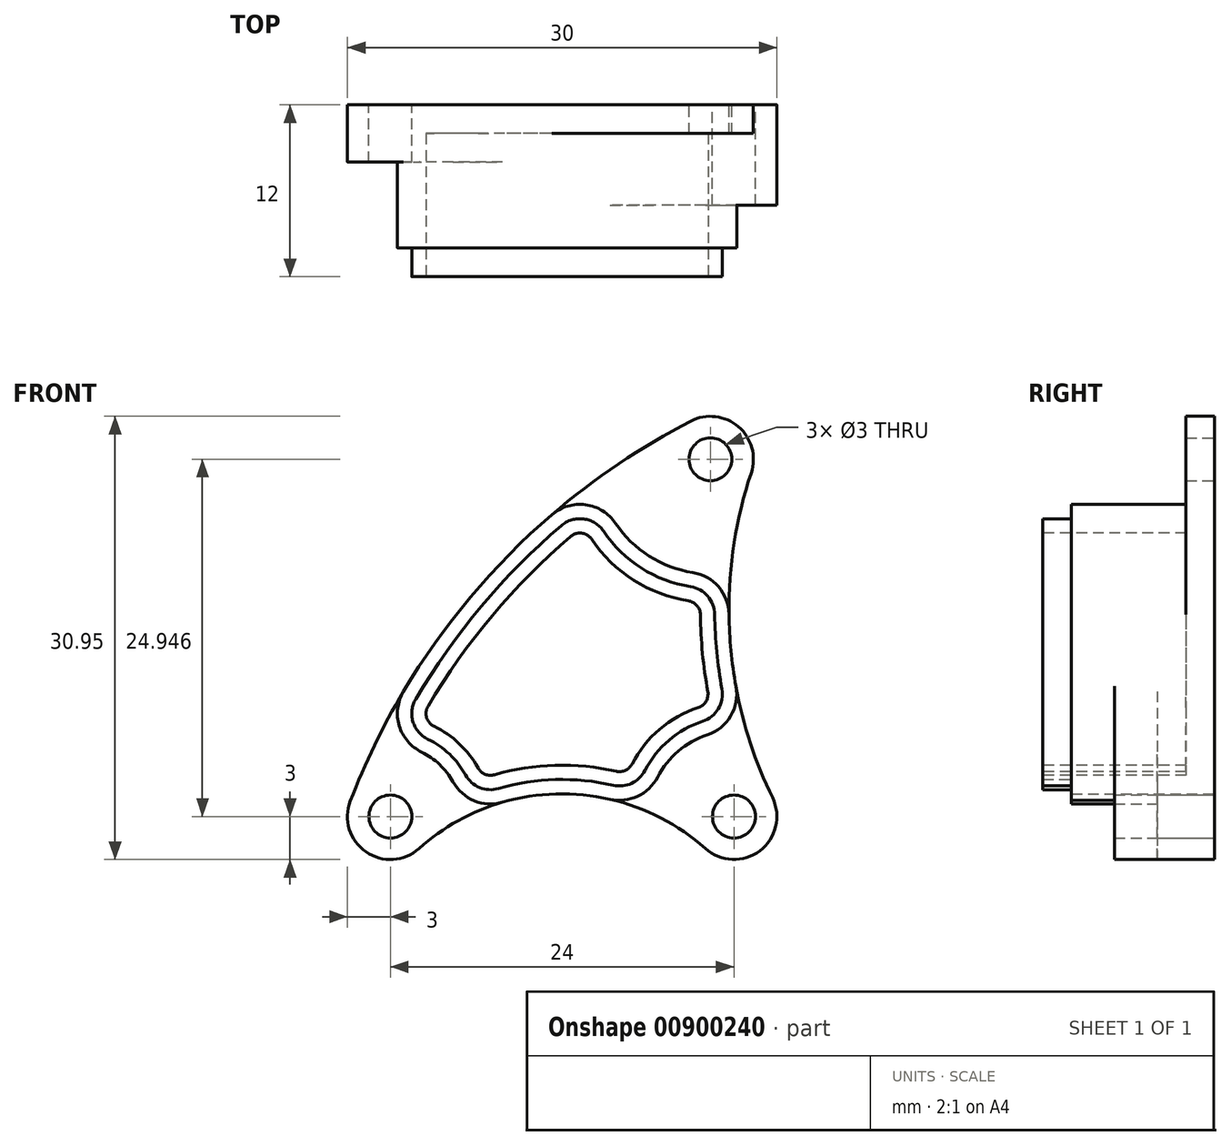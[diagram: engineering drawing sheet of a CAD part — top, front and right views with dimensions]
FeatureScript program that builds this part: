
annotation { "Feature Type Name" : "Feature", "Feature Type Description" : "" }
export const myFeature = defineFeature(function(context is Context, id is Id, definition is map)
    precondition{}
    {
        {
            var Q0;
            Q0=qCreatedBy(makeId("Front.planeOp"),FACE);
            var sketch = newSketch(context, id + "F0", { "sketchPlane" : qUnion([Q0])});
            skArc(sketch, "E0", {"start": v(-2.8, 1.07) * mm, "mid": v(-1.7, -2.47) * mm, "end": v(2, -2.24) * mm});
            skArc(sketch, "E1", {"start": v(25.2, 24) * mm, "mid": v(24.31, 27.22) * mm, "end": v(20.99, 27.61) * mm});
            skArc(sketch, "E2", {"start": v(22, -2.24) * mm, "mid": v(25.8, -2.4) * mm, "end": v(26.7, 1.32) * mm});
            skArc(sketch, "E3", {"start": v(20.99, 27.61) * mm, "mid": v(6.65, 16.54) * mm, "end": v(-2.8, 1.07) * mm});
            skArc(sketch, "E4", {"start": v(22, -2.24) * mm, "mid": v(12, 1.58) * mm, "end": v(2, -2.24) * mm});
            skArc(sketch, "E5", {"start": v(25.2, 24) * mm, "mid": v(23.72, 12.5) * mm, "end": v(26.7, 1.32) * mm});
            skSolve(sketch);
        }
        {
            var Q0;
            Q0=makeQuery(id+"F0.imprint","IMPRINT",FACE,{"disambiguationData":[TD([[makeQuery(id+"F0.imprint","IMPRINT",EDGE,{"derivedFrom":sQuery(id+"F0.wireOp",EDGE,"E0")}),1.0]])]});
            extrude(context, id + "F1", {"entities" : qUnion([Q0]), "depth" : 2 * mm, "offsetDistance" : 25 * mm});
        }
        {
            var Q0;
            Q0=makeQuery(id+"F1.opExtrude","CAP_FACE",FACE,{"disambiguationData":[OSD([sQuery(id+"F0.wireOp",EDGE,"E0"),sQuery(id+"F0.wireOp",EDGE,"E1"),sQuery(id+"F0.wireOp",EDGE,"E2"),sQuery(id+"F0.wireOp",EDGE,"E3"),sQuery(id+"F0.wireOp",EDGE,"E4"),sQuery(id+"F0.wireOp",EDGE,"E5")])],"isStart":false});
            var sketch = newSketch(context, id + "F2", { "sketchPlane" : qUnion([Q0])});
            skArc(sketch, "E6", {"start": v(4.37, 2.42) * mm, "mid": v(3.44, 3.63) * mm, "end": v(2.18, 4.5) * mm});
            skArc(sketch, "E7", {"start": v(22.13, 5.7) * mm, "mid": v(20.1, 4.57) * mm, "end": v(18.67, 2.75) * mm});
            skArc(sketch, "E8", {"start": v(15.72, 20.48) * mm, "mid": v(18.06, 18.2) * mm, "end": v(21.12, 17.04) * mm});
            skArc(sketch, "E9.0", {"start": v(11.28, 21.07) * mm, "mid": v(5.6, 15.32) * mm, "end": v(0.91, 8.73) * mm});
            skArc(sketch, "E10.0", {"start": v(23.66, 14.11) * mm, "mid": v(23.8, 11.6) * mm, "end": v(24.14, 9.09) * mm});
            skArc(sketch, "E11.0", {"start": v(15.34, 1.2) * mm, "mid": v(11.57, 1.58) * mm, "end": v(7.83, 1) * mm});
            skPoint(sketch, "E12.newPointA", {"position": v(-2.8, 1.07) * mm});
            skArc(sketch, "E12.filletArc", {"start": v(0.91, 8.73) * mm, "mid": v(0.62, 6.34) * mm, "end": v(2.18, 4.5) * mm});
            skPoint(sketch, "E13.newPointB", {"position": v(20.99, 27.61) * mm});
            skArc(sketch, "E13.filletArc", {"start": v(15.72, 20.48) * mm, "mid": v(13.64, 21.77) * mm, "end": v(11.28, 21.07) * mm});
            skPoint(sketch, "E14.newPointB", {"position": v(25.2, 24) * mm});
            skArc(sketch, "E14.filletArc", {"start": v(23.66, 14.11) * mm, "mid": v(22.92, 16.04) * mm, "end": v(21.12, 17.04) * mm});
            skPoint(sketch, "E15.newPointA", {"position": v(26.7, 1.32) * mm});
            skArc(sketch, "E15.filletArc", {"start": v(22.13, 5.7) * mm, "mid": v(23.77, 7.02) * mm, "end": v(24.14, 9.09) * mm});
            skPoint(sketch, "E16.newPointB", {"position": v(22, -2.24) * mm});
            skArc(sketch, "E16.filletArc", {"start": v(15.34, 1.2) * mm, "mid": v(17.27, 1.41) * mm, "end": v(18.67, 2.75) * mm});
            skPoint(sketch, "E17.newPointA", {"position": v(2, -2.24) * mm});
            skArc(sketch, "E17.filletArc", {"start": v(4.37, 2.42) * mm, "mid": v(5.85, 1.1) * mm, "end": v(7.83, 1) * mm});
            skSolve(sketch);
        }
        {
            var Q0;
            Q0=makeQuery(id+"F2.imprint","IMPRINT",FACE,{"disambiguationData":[TD([[makeQuery(id+"F2.imprint","IMPRINT",EDGE,{"derivedFrom":sQuery(id+"F2.wireOp",EDGE,"E6")}),-1.0]])]});
            extrude(context, id + "F3", {"entities" : qUnion([Q0]), "operationType" : NewBodyOperationType.ADD, "depth" : 8 * mm, "offsetDistance" : 25 * mm});
        }
        {
            var Q0;
            {var subQ0=sQuery(id+"F0.wireOp",EDGE,"E4");var subQ1=sQuery(id+"F0.wireOp",EDGE,"E3");var subQ2=sQuery(id+"F0.wireOp",EDGE,"E0");Q0=makeQuery(id+"F3.boolean.opBoolean","SPLIT",FACE,{"disambiguationData":[TD([makeQuery(id+"F1.opExtrude","SWEPT_FACE",FACE,{"disambiguationData":[OSD([subQ2])]})])],"derivedFrom":makeQuery(id+"F1.opExtrude","CAP_FACE",FACE,{"disambiguationData":[OSD([subQ2,sQuery(id+"F0.wireOp",EDGE,"E1"),sQuery(id+"F0.wireOp",EDGE,"E2"),subQ1,subQ0,sQuery(id+"F0.wireOp",EDGE,"E5")])],"isStart":false})});}
            var sketch = newSketch(context, id + "F4", { "sketchPlane" : qUnion([Q0])});
            skArc(sketch, "E18.0.0", {"start": v(7.83, 1) * mm, "mid": v(5.85, 1.1) * mm, "end": v(4.37, 2.42) * mm});
            skArc(sketch, "E18.0.1", {"start": v(4.37, 2.42) * mm, "mid": v(3.44, 3.63) * mm, "end": v(2.18, 4.5) * mm});
            skArc(sketch, "E18.0.2", {"start": v(2.18, 4.5) * mm, "mid": v(0.62, 6.34) * mm, "end": v(0.91, 8.73) * mm});
            skArc(sketch, "E18.0.3", {"start": v(0.91, 8.73) * mm, "mid": v(-1.1, 4.98) * mm, "end": v(-2.8, 1.07) * mm});
            skArc(sketch, "E18.0.4", {"start": v(-2.8, 1.07) * mm, "mid": v(-1.7, -2.47) * mm, "end": v(2, -2.24) * mm});
            skArc(sketch, "E18.0.5", {"start": v(2, -2.24) * mm, "mid": v(4.73, -0.3) * mm, "end": v(7.83, 1) * mm});
            skSolve(sketch);
        }
        {
            var Q0;
            Q0=makeQuery(id+"F4.imprint","IMPRINT",FACE,{"disambiguationData":[TD([[makeQuery(id+"F4.imprint","IMPRINT",EDGE,{"derivedFrom":sQuery(id+"F4.wireOp",EDGE,"E18.0.0")}),-1.0]])]});
            extrude(context, id + "F5", {"entities" : qUnion([Q0]), "operationType" : NewBodyOperationType.ADD, "depth" : 2 * mm, "offsetDistance" : 25 * mm});
        }
        {
            var Q0;
            {var subQ0=sQuery(id+"F0.wireOp",EDGE,"E5");var subQ1=sQuery(id+"F0.wireOp",EDGE,"E2");var subQ2=sQuery(id+"F0.wireOp",EDGE,"E4");Q0=makeQuery(id+"F3.boolean.opBoolean","SPLIT",FACE,{"disambiguationData":[TD([makeQuery(id+"F1.opExtrude","SWEPT_FACE",FACE,{"disambiguationData":[OSD([subQ1])]})])],"derivedFrom":makeQuery(id+"F1.opExtrude","CAP_FACE",FACE,{"disambiguationData":[OSD([sQuery(id+"F0.wireOp",EDGE,"E0"),sQuery(id+"F0.wireOp",EDGE,"E1"),subQ1,sQuery(id+"F0.wireOp",EDGE,"E3"),subQ2,subQ0])],"isStart":false})});}
            var sketch = newSketch(context, id + "F6", { "sketchPlane" : qUnion([Q0])});
            skArc(sketch, "E19.0.0", {"start": v(24.14, 9.09) * mm, "mid": v(23.77, 7.02) * mm, "end": v(22.13, 5.7) * mm});
            skArc(sketch, "E19.0.1", {"start": v(22.13, 5.7) * mm, "mid": v(20.1, 4.57) * mm, "end": v(18.67, 2.75) * mm});
            skArc(sketch, "E19.0.2", {"start": v(18.67, 2.75) * mm, "mid": v(17.27, 1.41) * mm, "end": v(15.34, 1.2) * mm});
            skArc(sketch, "E19.0.3", {"start": v(15.34, 1.2) * mm, "mid": v(18.89, -0.1) * mm, "end": v(22, -2.24) * mm});
            skArc(sketch, "E19.0.4", {"start": v(22, -2.24) * mm, "mid": v(25.8, -2.4) * mm, "end": v(26.7, 1.32) * mm});
            skArc(sketch, "E19.0.5", {"start": v(26.7, 1.32) * mm, "mid": v(25.15, 5.12) * mm, "end": v(24.14, 9.09) * mm});
            skSolve(sketch);
        }
        {
            var Q0;
            Q0=makeQuery(id+"F6.imprint","IMPRINT",FACE,{"disambiguationData":[TD([[makeQuery(id+"F6.imprint","IMPRINT",EDGE,{"derivedFrom":sQuery(id+"F6.wireOp",EDGE,"E19.0.0")}),-1.0]])]});
            extrude(context, id + "F7", {"entities" : qUnion([Q0]), "operationType" : NewBodyOperationType.ADD, "depth" : 5 * mm, "offsetDistance" : 25 * mm});
        }
        {
            var Q0;
            Q0=makeQuery(id+"F3.opExtrude","CAP_FACE",FACE,{"disambiguationData":[OSD([sQuery(id+"F2.wireOp",EDGE,"E6"),sQuery(id+"F2.wireOp",EDGE,"E7"),sQuery(id+"F2.wireOp",EDGE,"E8"),sQuery(id+"F2.wireOp",EDGE,"E9.0"),sQuery(id+"F2.wireOp",EDGE,"E10.0"),sQuery(id+"F2.wireOp",EDGE,"E11.0"),sQuery(id+"F2.wireOp",EDGE,"E12.filletArc"),sQuery(id+"F2.wireOp",EDGE,"E13.filletArc"),sQuery(id+"F2.wireOp",EDGE,"E14.filletArc"),sQuery(id+"F2.wireOp",EDGE,"E15.filletArc"),sQuery(id+"F2.wireOp",EDGE,"E16.filletArc"),sQuery(id+"F2.wireOp",EDGE,"E17.filletArc")])],"isStart":false});
            var sketch = newSketch(context, id + "F8", { "sketchPlane" : qUnion([Q0])});
            skArc(sketch, "E20.0", {"start": v(21.82, 6.65) * mm, "mid": v(22.91, 7.53) * mm, "end": v(23.16, 8.9) * mm});
            skArc(sketch, "E20.1", {"start": v(11.93, 20.32) * mm, "mid": v(6.36, 14.68) * mm, "end": v(1.77, 8.22) * mm});
            skArc(sketch, "E20.2", {"start": v(14.9, 19.92) * mm, "mid": v(13.5, 20.78) * mm, "end": v(11.93, 20.32) * mm});
            skArc(sketch, "E20.3", {"start": v(20.97, 16.05) * mm, "mid": v(17.53, 17.35) * mm, "end": v(14.9, 19.92) * mm});
            skArc(sketch, "E20.4", {"start": v(22.66, 14.1) * mm, "mid": v(22.17, 15.39) * mm, "end": v(20.97, 16.05) * mm});
            skArc(sketch, "E20.5", {"start": v(1.77, 8.22) * mm, "mid": v(1.58, 6.62) * mm, "end": v(2.62, 5.4) * mm});
            skArc(sketch, "E20.6", {"start": v(23.16, 8.9) * mm, "mid": v(22.8, 11.5) * mm, "end": v(22.66, 14.1) * mm});
            skArc(sketch, "E20.7", {"start": v(2.62, 5.4) * mm, "mid": v(4.13, 4.36) * mm, "end": v(5.25, 2.9) * mm});
            skArc(sketch, "E20.8", {"start": v(5.25, 2.9) * mm, "mid": v(6.24, 2.03) * mm, "end": v(7.55, 1.95) * mm});
            skArc(sketch, "E20.9", {"start": v(7.55, 1.95) * mm, "mid": v(11.54, 2.58) * mm, "end": v(15.56, 2.18) * mm});
            skArc(sketch, "E20.10", {"start": v(15.56, 2.18) * mm, "mid": v(16.85, 2.32) * mm, "end": v(17.78, 3.21) * mm});
            skArc(sketch, "E20.11", {"start": v(17.78, 3.21) * mm, "mid": v(19.46, 5.33) * mm, "end": v(21.82, 6.65) * mm});
            skSolve(sketch);
        }
        {
            var Q0;
            Q0=makeQuery(id+"F8.imprint","IMPRINT",FACE,{"disambiguationData":[TD([[makeQuery(id+"F8.imprint","IMPRINT",EDGE,{"derivedFrom":sQuery(id+"F8.wireOp",EDGE,"E20.0")}),1.0]])]});
            extrude(context, id + "F9", {"entities" : qUnion([Q0]), "operationType" : NewBodyOperationType.ADD, "depth" : 2 * mm, "offsetDistance" : 25 * mm});
        }
        {
            var Q0;
            Q0=makeQuery(id+"F9.opExtrude","CAP_FACE",FACE,{"disambiguationData":[OSD([sQuery(id+"F8.wireOp",EDGE,"E20.0"),sQuery(id+"F8.wireOp",EDGE,"E20.1"),sQuery(id+"F8.wireOp",EDGE,"E20.2"),sQuery(id+"F8.wireOp",EDGE,"E20.3"),sQuery(id+"F8.wireOp",EDGE,"E20.4"),sQuery(id+"F8.wireOp",EDGE,"E20.5"),sQuery(id+"F8.wireOp",EDGE,"E20.6"),sQuery(id+"F8.wireOp",EDGE,"E20.7"),sQuery(id+"F8.wireOp",EDGE,"E20.8"),sQuery(id+"F8.wireOp",EDGE,"E20.9"),sQuery(id+"F8.wireOp",EDGE,"E20.10"),sQuery(id+"F8.wireOp",EDGE,"E20.11")])],"isStart":false});
            var sketch = newSketch(context, id + "F10", { "sketchPlane" : qUnion([Q0])});
            skArc(sketch, "E21.0", {"start": v(12.58, 19.56) * mm, "mid": v(7.13, 14.04) * mm, "end": v(2.63, 7.7) * mm});
            skArc(sketch, "E21.1", {"start": v(15.78, 3.16) * mm, "mid": v(16.43, 3.23) * mm, "end": v(16.9, 3.67) * mm});
            skArc(sketch, "E21.2", {"start": v(7.28, 2.91) * mm, "mid": v(11.51, 3.58) * mm, "end": v(15.78, 3.16) * mm});
            skArc(sketch, "E21.3", {"start": v(6.12, 3.4) * mm, "mid": v(6.62, 2.95) * mm, "end": v(7.28, 2.91) * mm});
            skArc(sketch, "E21.4", {"start": v(3.05, 6.3) * mm, "mid": v(4.81, 5.08) * mm, "end": v(6.12, 3.4) * mm});
            skArc(sketch, "E21.5", {"start": v(16.9, 3.67) * mm, "mid": v(18.81, 6.09) * mm, "end": v(21.5, 7.6) * mm});
            skArc(sketch, "E21.6", {"start": v(2.63, 7.7) * mm, "mid": v(2.53, 6.91) * mm, "end": v(3.05, 6.3) * mm});
            skArc(sketch, "E21.7", {"start": v(21.5, 7.6) * mm, "mid": v(22.05, 8.04) * mm, "end": v(22.18, 8.73) * mm});
            skArc(sketch, "E21.8", {"start": v(22.18, 8.73) * mm, "mid": v(21.8, 11.4) * mm, "end": v(21.66, 14.1) * mm});
            skArc(sketch, "E21.9", {"start": v(21.66, 14.1) * mm, "mid": v(21.41, 14.73) * mm, "end": v(20.81, 15.07) * mm});
            skArc(sketch, "E21.10", {"start": v(20.81, 15.07) * mm, "mid": v(17, 16.5) * mm, "end": v(14.07, 19.36) * mm});
            skArc(sketch, "E21.11", {"start": v(14.07, 19.36) * mm, "mid": v(13.37, 19.8) * mm, "end": v(12.58, 19.56) * mm});
            skSolve(sketch);
        }
        {
            var Q0;
            Q0=makeQuery(id+"F10.imprint","IMPRINT",FACE,{"disambiguationData":[TD([[makeQuery(id+"F10.imprint","IMPRINT",EDGE,{"derivedFrom":sQuery(id+"F10.wireOp",EDGE,"E21.0")}),1.0]])]});
            extrude(context, id + "F11", {"entities" : qUnion([Q0]), "operationType" : NewBodyOperationType.REMOVE, "oppositeDirection" : true, "depth" : 10 * mm, "offsetDistance" : 25 * mm});
        }
        {
            var Q0;
            Q0=qCreatedBy(makeId("Front.planeOp"),FACE);
            var sketch = newSketch(context, id + "F12", { "sketchPlane" : qUnion([Q0])});
            skCircle(sketch, "E22", {"center": v(0, 0) * mm, "radius": 1.5 * mm});
            skCircle(sketch, "E23", {"center": v(22.36, 24.95) * mm, "radius": 1.5 * mm});
            skCircle(sketch, "E24", {"center": v(24, 0) * mm, "radius": 1.5 * mm});
            skSolve(sketch);
        }
        {
            var Q0;
            Q0 = qSketchRegion(id + "F12", true);
            extrude(context, id + "F13", {"entities" : qUnion([Q0]), "operationType" : NewBodyOperationType.REMOVE, "endBound" : BoundingType.THROUGH_ALL, "depth" : 25 * mm, "offsetDistance" : 25 * mm});
        }
    });
